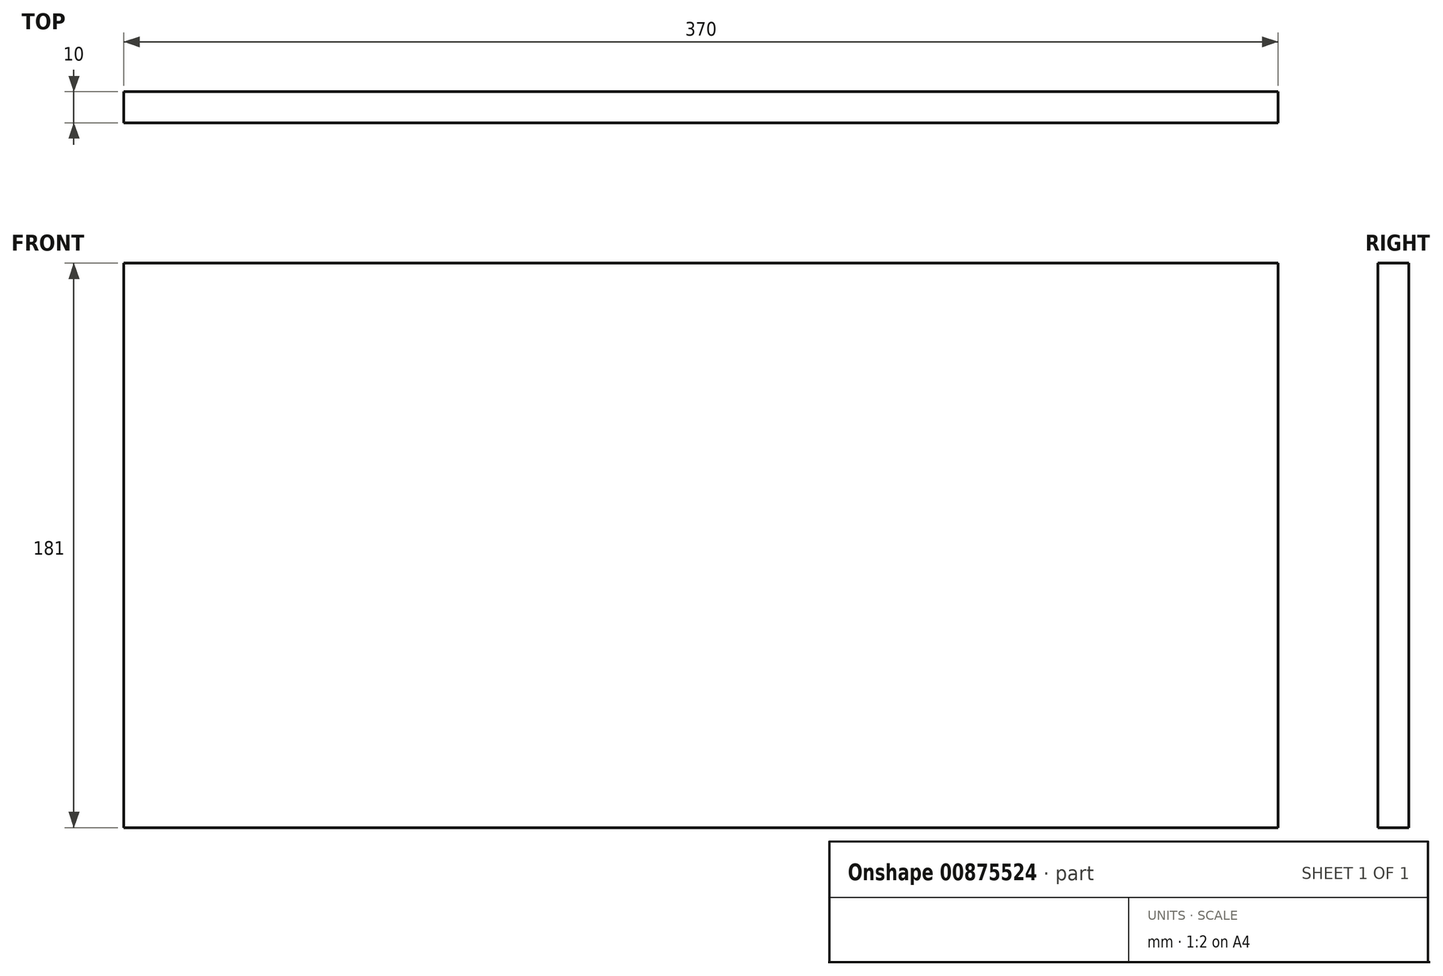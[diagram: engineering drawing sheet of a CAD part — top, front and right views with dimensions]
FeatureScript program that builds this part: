
annotation { "Feature Type Name" : "Feature", "Feature Type Description" : "" }
export const myFeature = defineFeature(function(context is Context, id is Id, definition is map)
    precondition{}
    {
        {
            var Q0;
            Q0=qCreatedBy(makeId("Front.planeOp"),FACE);
            var sketch = newSketch(context, id + "F0", { "sketchPlane" : qUnion([Q0])});
            skLineSegment(sketch, "E0.bottom", {"start": v(241.05, 83.89) * mm, "end": v(-128.95, 83.89) * mm});
            skLineSegment(sketch, "E0.top", {"start": v(241.05, -97.11) * mm, "end": v(-128.95, -97.11) * mm});
            skLineSegment(sketch, "E0.left", {"start": v(241.05, 83.89) * mm, "end": v(241.05, -97.11) * mm});
            skLineSegment(sketch, "E0.right", {"start": v(-128.95, 83.89) * mm, "end": v(-128.95, -97.11) * mm});
            skSolve(sketch);
        }
        {
            var Q0;
            Q0=makeQuery(id+"F0.imprint","IMPRINT",FACE,{"disambiguationData":[TD([[makeQuery(id+"F0.imprint","IMPRINT",EDGE,{"derivedFrom":sQuery(id+"F0.wireOp",EDGE,"E0.bottom")}),1.0]])]});
            extrude(context, id + "F1", {"entities" : qUnion([Q0]), "depth" : 10 * mm, "offsetDistance" : 25 * mm});
        }
    });
